# Revit family: Gira_109203
name_source: partatom
category: Elektroinstallationen
revit_build: Autodesk Revit 2017 (Build: 20160225_1515(x64)
units: mm (PartAtom-declared; Revit-internal decimal feet)

## family parameters
Basisbauteil = Fläche
Beim Laden mit Abzugskörper schneiden = Nein
Bemaßung runder Anschluss = Durchmesser verwenden
Beschriftungsausrichtung beibehalten = Nein
Gemeinsam genutzt = Nein
Raumberechnungspunkt = Nein
Teiletyp = Normal

## types (1)
- Gira_109203
    Anzahl der Einheiten = 2
    Anzahl der Einheiten horizontal = 2
    Anzahl der Einheiten vertikal = 1
    Ausführung der Oberfläche = glänzend
    BIM = https://media.stage.bim.site
    Bauelement = Espr._Rahmen_1fach
    Befestigungsart = Klemmbefestigung
    Beschreibung = Abdeckrahmen Gira Standard 55 mit Beschriftungsfeld Reinweiß glänzend 2fach waagerecht Merkmale: - Bruchsicher. - Sprühnebeldicht. - Abdeckrahmen mit transparentem Sichtfenster zur Beschriftung der Einsätze. - Besonders geeignet für Objekte, in denen Elektroinstallation gekennzeichnet und dokumentiert werden muss, bspw. in Verwaltungen, gewerblichen Betrieben, Flughäfen, Unternehmen und Krankenhäusern.  Hinweise : - Nicht zu verwenden mit: Dichtungsset IP44, Aufputz-Gehäuse flache Bauweise, Aufputz-Gehäuse.
    Datenblatt = https://katalog.gira.de
    Farbe = weiß
    GTIN = 4010337092032
    Geeignet für Einbauinstallation = Nein
    Geeignet für Geräteeinbaukanal = Nein
    Geeignet für Unterflurkanaldose = Nein
    Geeignet für Unterputz-Installation = Ja
    HAN = 109203
    Halogenfrei = Ja
    Hersteller = Gira
    Mit Klappdeckel = Nein
    Mit Montagerahmen = Nein
    Montagerichtung = horizontal
    Oberfläche = sonstige
    Produktseite = http://katalog.gira.de
    RAL-Nummer (ähnlich) = 9010
    Schutzart (IP) = IP20
    Textfeld/Beschriftungsfläche = Ja
    Transparent = Nein
    Typname = Abdeckrahmen 2f waager. BSF Standard 55 Reinweiß
    URL = https://www.gira.de
    Vorgabe-Ansicht = 1219 mm
    Werkstoff = Kunststoff
    Werkstoffgüte = Thermoplast

## geometry (parser evidence)
native form markers: Sweep x2
no freeform markers — native parametric forms only
